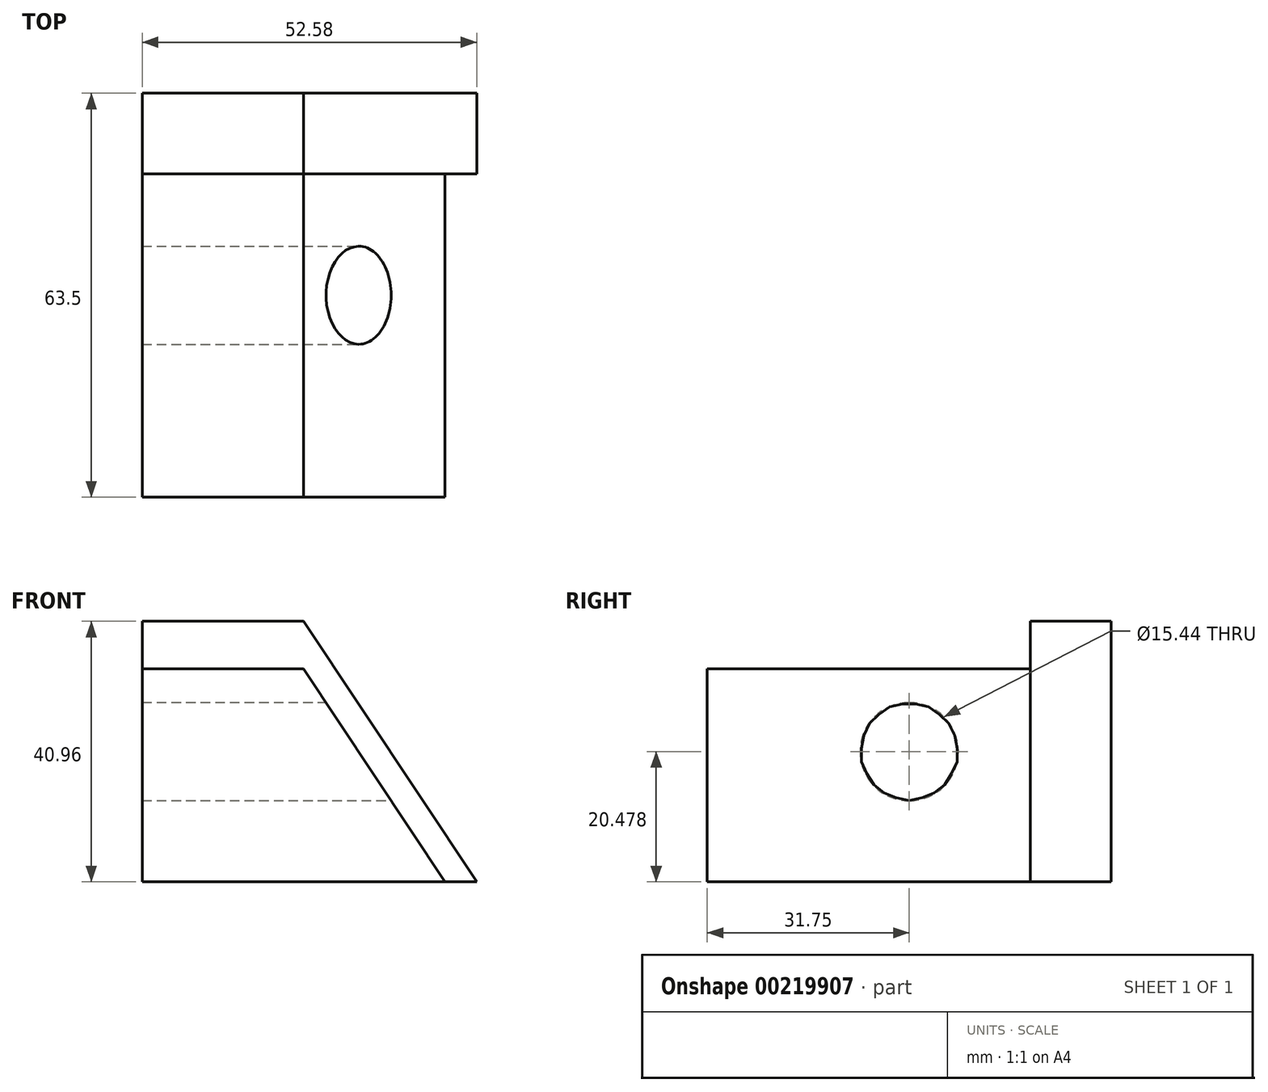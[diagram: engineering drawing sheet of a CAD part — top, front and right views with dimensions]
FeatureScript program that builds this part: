
annotation { "Feature Type Name" : "Feature", "Feature Type Description" : "" }
export const myFeature = defineFeature(function(context is Context, id is Id, definition is map)
    precondition{}
    {
        {
            var Q0;
            Q0=qCreatedBy(makeId("Front.planeOp"),FACE);
            var sketch = newSketch(context, id + "F0", { "sketchPlane" : qUnion([Q0])});
            skLineSegment(sketch, "E0", {"start": v(0, 0) * mm, "end": v(-52.58, 0) * mm});
            skLineSegment(sketch, "E1", {"start": v(-52.58, 0) * mm, "end": v(-52.58, 40.96) * mm});
            skLineSegment(sketch, "E2", {"start": v(-52.58, 40.96) * mm, "end": v(-27.18, 40.96) * mm});
            skLineSegment(sketch, "E3", {"start": v(-27.18, 40.96) * mm, "end": v(0, 0) * mm});
            skSolve(sketch);
        }
        {
            var Q0;
            Q0=makeQuery(id+"F0.imprint","IMPRINT",FACE,{"disambiguationData":[TD([[makeQuery(id+"F0.imprint","IMPRINT",EDGE,{"derivedFrom":sQuery(id+"F0.wireOp",EDGE,"E0")}),-1.0]])]});
            extrude(context, id + "F1", {"entities" : qUnion([Q0]), "depth" : 63.5 * mm});
        }
        {
            var Q0;
            Q0=qCreatedBy(makeId("Right.planeOp"),FACE);
            var sketch = newSketch(context, id + "F2", { "sketchPlane" : qUnion([Q0])});
            skPoint(sketch, "E4.0", {"position": v(-31.75, 40.96) * mm});
            skPoint(sketch, "E5.0", {"position": v(0, 20.48) * mm});
            skCircle(sketch, "E6", {"center": v(-31.75, 20.48) * mm, "radius": 7.72 * mm});
            skSolve(sketch);
        }
        {
            var Q0;
            Q0=makeQuery(id+"F2.imprint","IMPRINT",FACE,{"disambiguationData":[TD([[makeQuery(id+"F2.imprint","IMPRINT",EDGE,{"derivedFrom":sQuery(id+"F2.wireOp",EDGE,"E6")}),1.0]])]});
            extrude(context, id + "F3", {"entities" : qUnion([Q0]), "operationType" : NewBodyOperationType.REMOVE, "endBound" : BoundingType.THROUGH_ALL, "oppositeDirection" : true, "depth" : 25.4 * mm});
        }
        {
            var Q0;
            Q0=makeQuery(id+"F1.opExtrude","CAP_FACE",FACE,{"disambiguationData":[OSD([sQuery(id+"F0.wireOp",EDGE,"E0"),sQuery(id+"F0.wireOp",EDGE,"E1"),sQuery(id+"F0.wireOp",EDGE,"E2"),sQuery(id+"F0.wireOp",EDGE,"E3")])],"isStart":false});
            var sketch = newSketch(context, id + "F4", { "sketchPlane" : qUnion([Q0])});
            skPoint(sketch, "E7.0", {"position": v(-52.58, 40.96) * mm});
            skPoint(sketch, "E8.0", {"position": v(-27.18, 40.96) * mm});
            skPoint(sketch, "E9.0", {"position": v(0, 0) * mm});
            skLineSegment(sketch, "E10", {"start": v(-52.58, 0) * mm, "end": v(-52.58, 33.48) * mm});
            skLineSegment(sketch, "E11", {"start": v(-52.58, 33.48) * mm, "end": v(-27.18, 33.48) * mm});
            skLineSegment(sketch, "E12", {"start": v(-27.18, 33.48) * mm, "end": v(-4.96, 0) * mm});
            skSolve(sketch);
        }
        {
            var Q0;
            {var subQ2=sQuery(id+"F4.wireOp",EDGE,"E11");Q0=makeQuery(id+"F4.imprint","IMPRINT",FACE,{"disambiguationData":[TD([[makeQuery(id+"F4.imprint","IMPRINT",EDGE,{"derivedFrom":subQ2}),1.0]])]});}
            extrude(context, id + "F5", {"entities" : qUnion([Q0]), "operationType" : NewBodyOperationType.REMOVE, "oppositeDirection" : true, "depth" : 50.8 * mm});
        }
    });
